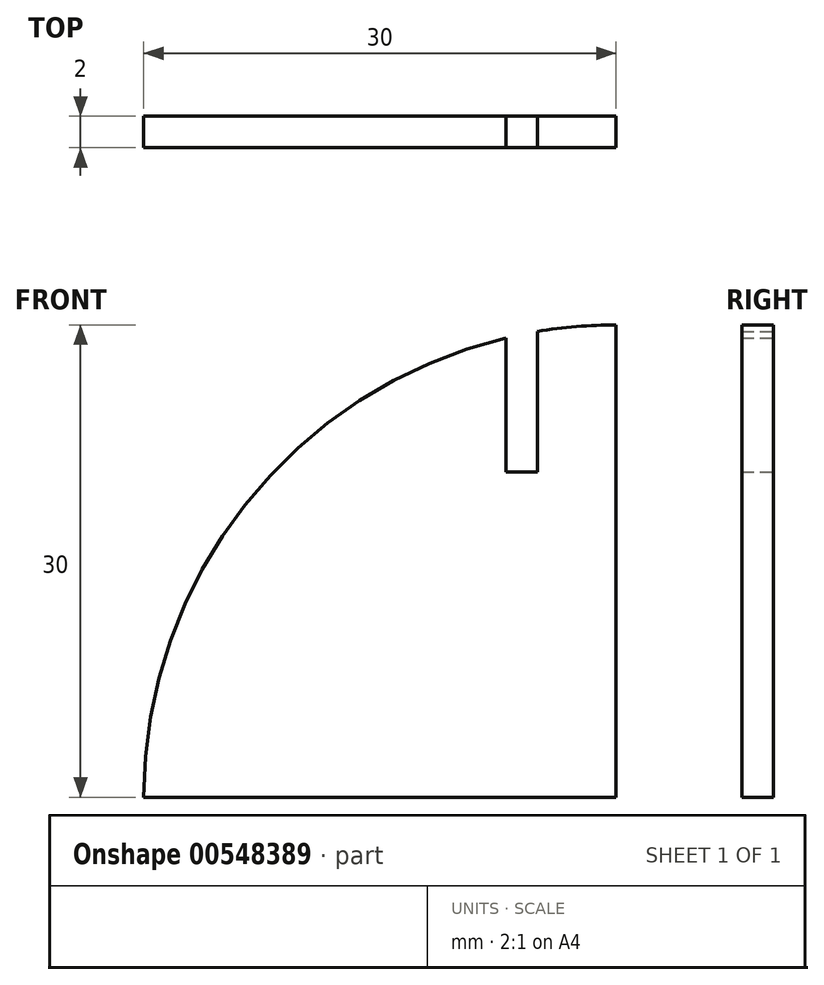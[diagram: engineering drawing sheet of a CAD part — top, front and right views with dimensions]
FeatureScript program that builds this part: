
annotation { "Feature Type Name" : "Feature", "Feature Type Description" : "" }
export const myFeature = defineFeature(function(context is Context, id is Id, definition is map)
    precondition{}
    {
        {
            var Q0;
            Q0=qCreatedBy(makeId("Front.planeOp"),FACE);
            var sketch = newSketch(context, id + "F0", { "sketchPlane" : qUnion([Q0])});
            skArc(sketch, "E0", {"start": v(-30, 0) * mm, "mid": v(-21.21, 21.21) * mm, "end": v(0, 30) * mm});
            skLineSegment(sketch, "E1", {"start": v(0, 30) * mm, "end": v(0, 0) * mm});
            skLineSegment(sketch, "E2", {"start": v(-30, 0) * mm, "end": v(0, 0) * mm});
            skSolve(sketch);
        }
        {
            var Q0;
            Q0=qSketchRegion(id+"F0",true);
            extrude(context, id + "F1", {"entities" : qUnion([Q0]), "depth" : 2 * mm});
        }
        {
            var Q0;
            Q0=qCreatedBy(makeId("Front.planeOp"),FACE);
            var sketch = newSketch(context, id + "F2", { "sketchPlane" : qUnion([Q0])});
            skLineSegment(sketch, "E3.top", {"start": v(-5, 52.1) * mm, "end": v(-7, 52.1) * mm});
            skLineSegment(sketch, "E3.left", {"start": v(-5, 20.66) * mm, "end": v(-5, 52.1) * mm});
            skLineSegment(sketch, "E3.right", {"start": v(-7, 20.66) * mm, "end": v(-7, 52.1) * mm});
            skLineSegment(sketch, "E4", {"start": v(-7, 20.66) * mm, "end": v(-5, 20.66) * mm});
            skSolve(sketch);
        }
        {
            var Q0;
            Q0=qSketchRegion(id+"F2",true);
            extrude(context, id + "F3", {"entities" : qUnion([Q0]), "operationType" : NewBodyOperationType.REMOVE, "depth" : 25 * mm});
        }
    });
